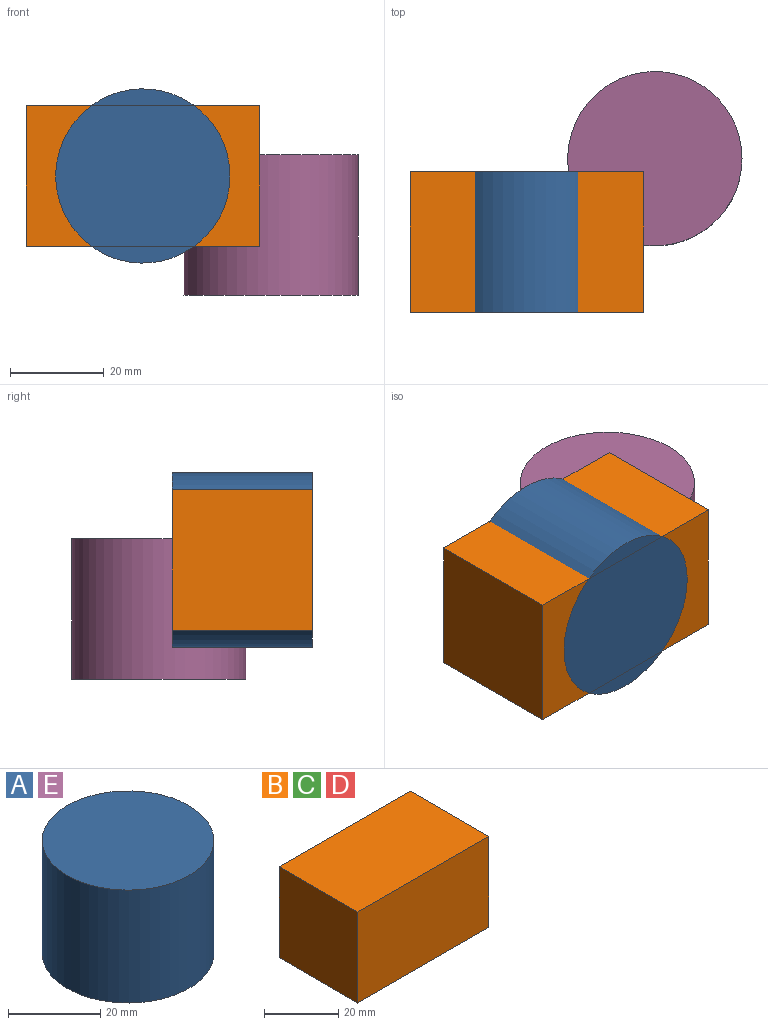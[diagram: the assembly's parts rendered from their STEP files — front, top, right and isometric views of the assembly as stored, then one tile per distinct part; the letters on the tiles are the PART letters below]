
ASSEMBLY  parts=5 mates=1
PART A: 3 faces, bbox 37.3x37.3x30 mm
  f0: cylinder r=18.64mm len=37.27mm, axis (0,0,-1), area 3513.1mm2, adj f1,f2
  f1: plane 37.27x37.27mm, normal (0,0,1), area 1091.2mm2, adj f0
  f2: plane 37.27x37.27mm, normal (0,0,-1), area 1091.2mm2, adj f0
PART B: 6 faces, bbox 50x30x30 mm
  f0: plane 50x30mm, normal (0,1,0), area 1500mm2, adj f1,f3,f4,f5
  f1: plane 30x30mm, normal (-1,0,0), area 900mm2, adj f0,f2,f4,f5
  f2: plane 50x30mm, normal (0,-1,0), area 1500mm2, adj f1,f3,f4,f5
  f3: plane 30x30mm, normal (1,0,0), area 900mm2, adj f0,f2,f4,f5
  f4: plane 50x30mm, normal (0,0,1), area 1500mm2, adj f0,f1,f2,f3
  f5: plane 50x30mm, normal (0,0,-1), area 1500mm2, adj f0,f1,f2,f3
PART C: same geometry as B
PART D: same geometry as B
PART E: same geometry as A
PLACE A rot(axis=(1,0,0),90deg) t=(63.82,-4.09,1.95)mm
PLACE B t=(-4.73,13.94,-19.47)mm
PLACE C t=(-4.73,13.94,-19.47)mm
PLACE D t=(-4.73,13.94,-19.47)mm
PLACE E t=(91.2,5.19,-29.95)mm
MATE cylindrical A.f0 <-> B.f2  axis (0,-1,0) through (-27.89,-34.09,-4.47)mm
